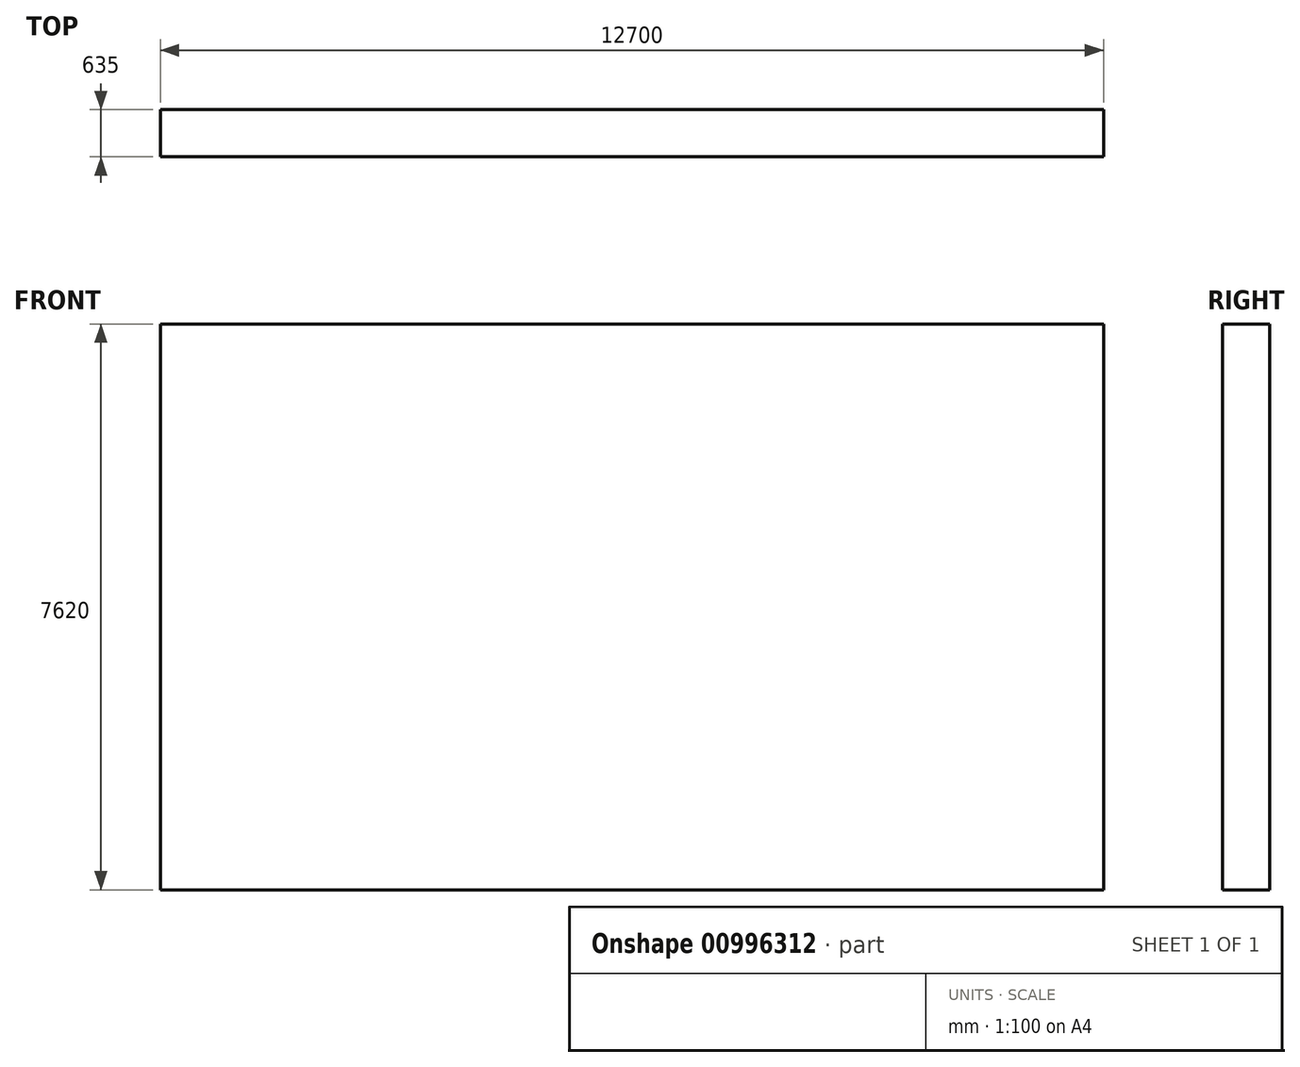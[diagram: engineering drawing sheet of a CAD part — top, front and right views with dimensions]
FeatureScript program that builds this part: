
annotation { "Feature Type Name" : "Feature", "Feature Type Description" : "" }
export const myFeature = defineFeature(function(context is Context, id is Id, definition is map)
    precondition{}
    {
        {
            var Q0;
            Q0=qCreatedBy(makeId("Front.planeOp"),FACE);
            var sketch = newSketch(context, id + "F0", { "sketchPlane" : qUnion([Q0])});
            skLineSegment(sketch, "E0.bottom", {"start": v(0, 0) * mm, "end": v(12700, 0) * mm});
            skLineSegment(sketch, "E0.top", {"start": v(0, -7620) * mm, "end": v(12700, -7620) * mm});
            skLineSegment(sketch, "E0.left", {"start": v(0, 0) * mm, "end": v(0, -7620) * mm});
            skLineSegment(sketch, "E0.right", {"start": v(12700, 0) * mm, "end": v(12700, -7620) * mm});
            skSolve(sketch);
        }
        {
            var Q0;
            Q0 = qSketchRegion(id + "F0", true);
            extrude(context, id + "F1", {"entities" : qUnion([Q0]), "depth" : 635 * mm, "offsetDistance" : 25.4 * mm});
        }
    });
